# Revit family: Urbane II Hob Swivel Outlet 210mm
name_source: partatom
category: Specialty Equipment
units: mm (PartAtom-declared; Revit-internal decimal feet)

## family parameters
Cut with Voids When Loaded = No
Host = Face
OmniClass Number = 23.45.55.14
OmniClass Title = Single Faucets
Part Type = Normal
Room Calculation Point = No
Round Connector Dimension = Use Radius
Shared = No

## types (5) — shared parameters
Assembly Code = C1030220
Default Elevation = 1000 mm  [stored 3.28084 ft]
Manufacturer = GWA Bathrooms & Kitchens
URL = https://www.caroma.com.au

## per-type parameters (varying)
| type | Material_Base | Model |
| Urbane II Hob Swivel Outlet 210mm – Chrome | GWA_Metal-Chrome | 99685C65A |
| Urbane II Hob Swivel Outlet 210mm – Matte Black | GWA-Metal-Black | 99685B65A |
| Urbane II Hob Swivel Outlet 210mm – Brushed Brass | GWA_Metal-Brushed-Brass | 99685BB65A |
| Urbane II Hob Swivel Outlet 210mm – Gunmetal | GWA-Metal-Gunmetal Grey | 99685GM65A |
| Urbane II Hob Swivel Outlet 210mm – Brushed Nickel | GWA_Metal-Brushed-Nickel | 99685BN65A |

note: column(s) folded — value = type name in every type: Description

note: [stored X ft] marks values corroborated as IEEE doubles in the binary element streams (Revit-internal decimal feet)

## geometry (parser evidence)
native form markers: Sweep x2
no freeform markers — native parametric forms only
